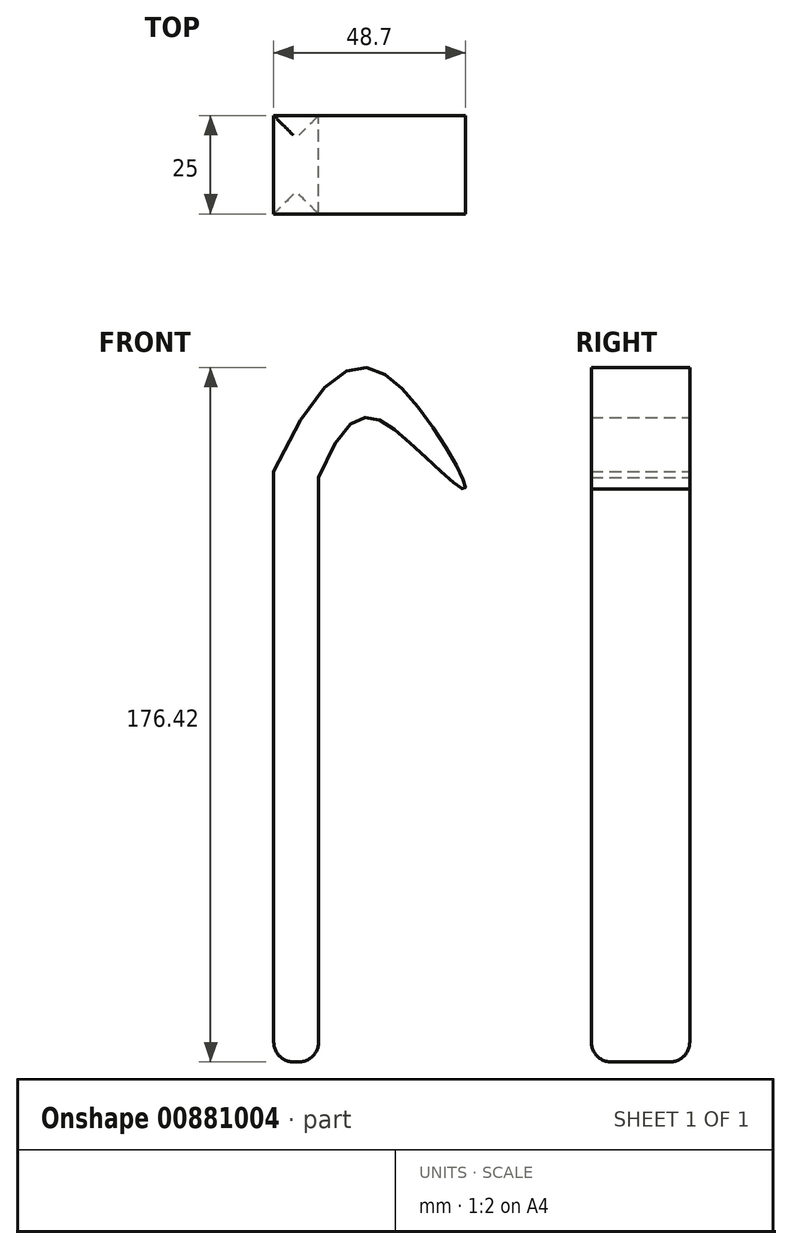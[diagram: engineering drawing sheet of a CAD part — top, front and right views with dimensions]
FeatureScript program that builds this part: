
annotation { "Feature Type Name" : "Feature", "Feature Type Description" : "" }
export const myFeature = defineFeature(function(context is Context, id is Id, definition is map)
    precondition{}
    {
        {
            var Q0;
            Q0=qCreatedBy(makeId("Front.planeOp"),FACE);
            var sketch = newSketch(context, id + "F0", { "sketchPlane" : qUnion([Q0])});
            skLineSegment(sketch, "E0", {"start": v(-63.62, 8.6) * mm, "end": v(-63.62, -141.4) * mm});
            skLineSegment(sketch, "E1", {"start": v(-63.62, -141.4) * mm, "end": v(-52.22, -141.4) * mm});
            skLineSegment(sketch, "E2", {"start": v(-52.22, -141.4) * mm, "end": v(-52.22, 7.1) * mm});
            skFitSpline(sketch, "E3", {"points": [v(-52.22, 7.1) * mm, v(-31.43, 18) * mm, v(-15.14, 4.1) * mm, v(-26.7, 24.64) * mm, v(-63.62, 8.6) * mm], "startDerivative": vector(100.3, 248.73) * mm, "endDerivative": vector(-163.27, -360.57) * mm});
            skSolve(sketch);
        }
        {
            var Q0;
            Q0 = qSketchRegion(id + "F0", true);
            extrude(context, id + "F1", {"entities" : qUnion([Q0]), "depth" : 25 * mm, "offsetDistance" : 25 * mm});
        }
        {
            var Q0;
            Q0=makeQuery(id+"F1.opExtrude","SWEPT_FACE",FACE,{"disambiguationData":[OSD([sQuery(id+"F0.wireOp",EDGE,"E1")])]});
            fillet(context, id + "F2", {"entities" : qUnion([Q0]), "radius" : 5 * mm, "tangentPropagation" : true, "allowEdgeOverflow" : false});
        }
    });
